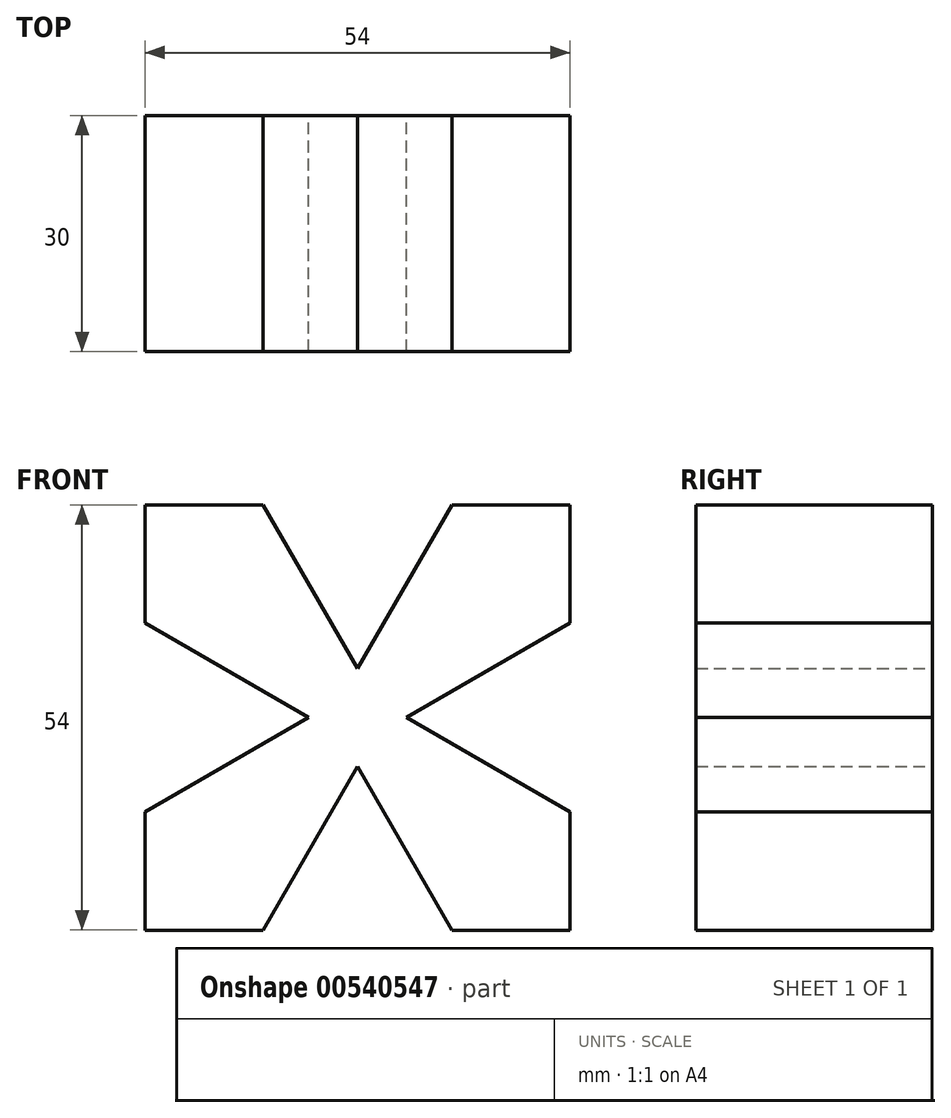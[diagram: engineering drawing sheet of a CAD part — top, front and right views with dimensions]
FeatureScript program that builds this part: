
annotation { "Feature Type Name" : "Feature", "Feature Type Description" : "" }
export const myFeature = defineFeature(function(context is Context, id is Id, definition is map)
    precondition{}
    {
        {
            var Q0;
            Q0=qCreatedBy(makeId("Front.planeOp"),FACE);
            var sketch = newSketch(context, id + "F0", { "sketchPlane" : qUnion([Q0])});
            skLineSegment(sketch, "E0", {"start": v(0, 0) * mm, "end": v(-12, -20.78) * mm});
            skLineSegment(sketch, "E1", {"start": v(-12, -20.78) * mm, "end": v(-27, -20.78) * mm});
            skLineSegment(sketch, "E2", {"start": v(-27, -20.78) * mm, "end": v(-27, -5.78) * mm});
            skLineSegment(sketch, "E3", {"start": v(-27, -5.78) * mm, "end": v(-6.22, 6.22) * mm});
            skLineSegment(sketch, "E4", {"start": v(-6.22, 6.22) * mm, "end": v(-27, 18.22) * mm});
            skLineSegment(sketch, "E5", {"start": v(-27, 18.22) * mm, "end": v(-27, 33.22) * mm});
            skLineSegment(sketch, "E6", {"start": v(-27, 33.22) * mm, "end": v(-12, 33.22) * mm});
            skLineSegment(sketch, "E7", {"start": v(-12, 33.22) * mm, "end": v(0, 12.43) * mm});
            skLineSegment(sketch, "E8", {"start": v(0, 12.43) * mm, "end": v(12, 33.22) * mm});
            skLineSegment(sketch, "E9", {"start": v(12, 33.22) * mm, "end": v(27, 33.22) * mm});
            skLineSegment(sketch, "E10", {"start": v(27, 33.22) * mm, "end": v(27, 18.22) * mm});
            skLineSegment(sketch, "E11", {"start": v(27, 18.22) * mm, "end": v(6.22, 6.22) * mm});
            skLineSegment(sketch, "E12", {"start": v(6.22, 6.22) * mm, "end": v(27, -5.78) * mm});
            skLineSegment(sketch, "E13", {"start": v(27, -5.78) * mm, "end": v(27, -20.78) * mm});
            skLineSegment(sketch, "E14", {"start": v(27, -20.78) * mm, "end": v(12, -20.78) * mm});
            skLineSegment(sketch, "E15", {"start": v(12, -20.78) * mm, "end": v(0, 0) * mm});
            skLineSegment(sketch, "E16", {"start": v(-12, -20.78) * mm, "end": v(12, -20.78) * mm, "construction": true});
            skLineSegment(sketch, "E17", {"start": v(27, -5.78) * mm, "end": v(27, 18.22) * mm, "construction": true});
            skLineSegment(sketch, "E18", {"start": v(12, 33.22) * mm, "end": v(-12, 33.22) * mm, "construction": true});
            skLineSegment(sketch, "E19", {"start": v(-27, 18.22) * mm, "end": v(-27, -5.78) * mm, "construction": true});
            skSolve(sketch);
        }
        {
            var Q0;
            Q0 = qSketchRegion(id + "F0", true);
            extrude(context, id + "F1", {"entities" : qUnion([Q0]), "depth" : 30 * mm, "offsetDistance" : 25 * mm});
        }
    });
